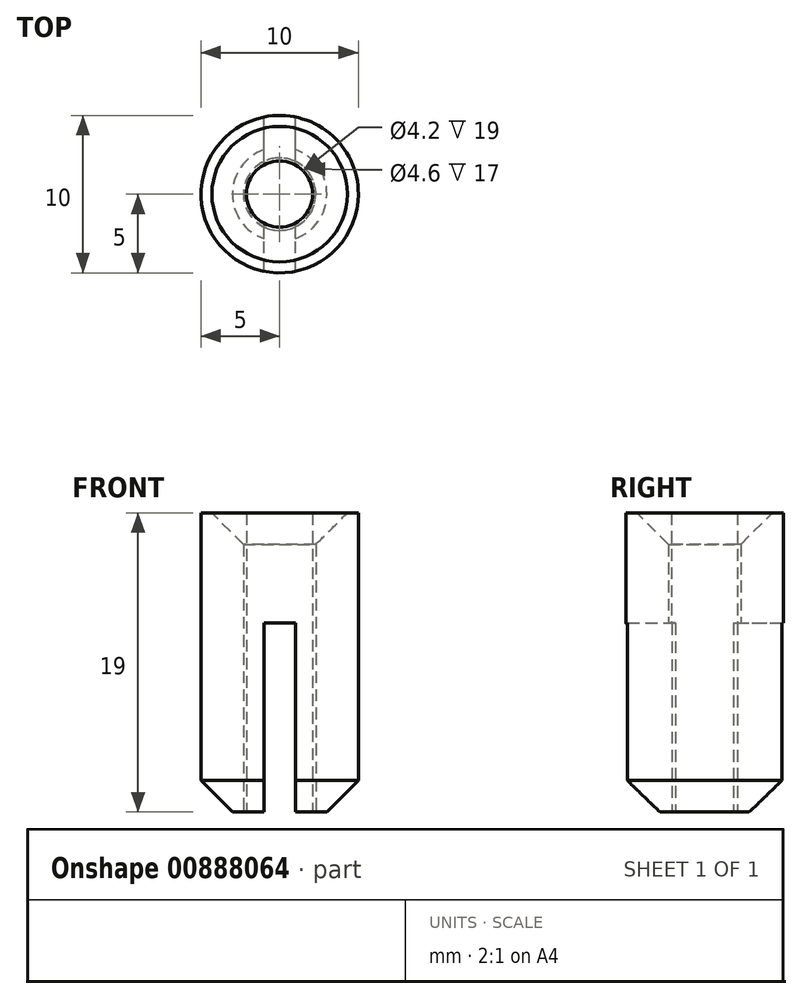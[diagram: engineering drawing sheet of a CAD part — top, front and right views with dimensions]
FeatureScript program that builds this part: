
annotation { "Feature Type Name" : "Feature", "Feature Type Description" : "" }
export const myFeature = defineFeature(function(context is Context, id is Id, definition is map)
    precondition{}
    {
        {
            var Q0;
            Q0=qCreatedBy(makeId("Top.planeOp"),FACE);
            var sketch = newSketch(context, id + "F0", { "sketchPlane" : qUnion([Q0])});
            skCircle(sketch, "E0", {"center": v(0, 0) * mm, "radius": 2.3 * mm});
            skCircle(sketch, "E1", {"center": v(0, 0) * mm, "radius": 5 * mm});
            skSolve(sketch);
        }
        {
            var Q0;
            Q0 = qSketchRegion(id + "F0", true);
            extrude(context, id + "F1", {"entities" : qUnion([Q0]), "depth" : 19 * mm, "offsetDistance" : 25 * mm});
        }
        {
            var Q0;
            Q0=makeQuery(id+"F1.opExtrude","CAP_EDGE",EDGE,{"disambiguationData":[OSD([sQuery(id+"F0.wireOp",EDGE,"E0")])],"isStart":false});
            var Q1;
            Q1=makeQuery(id+"F1.opExtrude","CAP_EDGE",EDGE,{"disambiguationData":[OSD([sQuery(id+"F0.wireOp",EDGE,"E1")])],"isStart":true});
            chamfer(context, id + "F2", {"entities" : qUnion([Q0, Q1]), "width" : 2 * mm, "tangentPropagation" : true});
        }
        {
            var Q0;
            Q0=qCreatedBy(makeId("Top.planeOp"),FACE);
            var sketch = newSketch(context, id + "F3", { "sketchPlane" : qUnion([Q0])});
            skCircle(sketch, "E2", {"center": v(0, 0) * mm, "radius": 5 * mm});
            skSolve(sketch);
        }
        {
            var Q0;
            Q0 = qSketchRegion(id + "F3", true);
            extrude(context, id + "F4", {"entities" : qUnion([Q0]), "depth" : 19 * mm, "offsetDistance" : 25 * mm});
        }
        {
            var Q0;
            Q0=makeQuery(id+"F4.opExtrude","CAP_FACE",FACE,{"disambiguationData":[OSD([sQuery(id+"F3.wireOp",EDGE,"E2")])],"isStart":false});
            var sketch = newSketch(context, id + "F5", { "sketchPlane" : qUnion([Q0])});
            skPoint(sketch, "E3", {"position": v(0, 0) * mm});
            skSolve(sketch);
        }
        {
            var Q0;
            Q0=sQuery(id+"F5.wireOp",VERTEX,"E3");
            var Q1;
            Q1=makeQuery(id+"F4.opExtrude","SWEPT_BODY",BODY,{"disambiguationData":[OSD([sQuery(id+"F3.wireOp",EDGE,"E2")])]});
            hole(context, id + "F6", {"style" : HoleStyle.SIMPLE, "endStyle" : HoleEndStyle.THROUGH, "standardTappedOrClearance" : lookupTablePath({ "standard" : "ISO", "engagement" : "75%", "pitch" : "0.8 mm", "size" : "M5", "type" : "Tapped" }), "standardBlindInLast" : lookupTablePath({ "standard" : "ISO", "fit" : "Normal", "engagement" : "75%", "pitch" : "0.8 mm", "size" : "M5", "type" : "Clearance & tapped" }), "holeDiameter" : 4.2 * mm, "majorDiameter" : 5 * mm, "showTappedDepth" : true, "isTappedThrough" : true, "tappedDepth" : 12 * mm, "tapClearance" : 3, "locations" : qUnion([Q0]), "scope" : qUnion([Q1]), "startStyle" : HoleStartStyle.PART});
        }
        {
            var Q0;
            Q0=makeQuery(id+"F6.hole-0.boolean.opBoolean","COPY",EDGE,{"derivedFrom":makeQuery(id+"F6.hole-0.opRevolve","SWEPT_EDGE",EDGE,{"disambiguationData":[OSD([sQuery(id+"F6.hole-0.sketch.wireOp",EDGE,"core_line_2"),sQuery(id+"F6.hole-0.sketch.wireOp",EDGE,"core_line_3")])]})});
            var Q1;
            Q1=makeQuery(id+"F4.opExtrude","CAP_EDGE",EDGE,{"disambiguationData":[OSD([sQuery(id+"F3.wireOp",EDGE,"E2")])],"isStart":true});
            chamfer(context, id + "F7", {"entities" : qUnion([Q0, Q1]), "width" : 2 * mm, "tangentPropagation" : true});
        }
        {
            var Q0;
            Q0=makeQuery(id+"F4.opExtrude","CAP_FACE",FACE,{"disambiguationData":[OSD([sQuery(id+"F3.wireOp",EDGE,"E2")])],"isStart":true});
            var sketch = newSketch(context, id + "F8", { "sketchPlane" : qUnion([Q0])});
            skLineSegment(sketch, "E4.bottom", {"start": v(0.5, 6) * mm, "end": v(-0.5, 6) * mm});
            skLineSegment(sketch, "E4.top", {"start": v(0.5, -6) * mm, "end": v(-0.5, -6) * mm});
            skLineSegment(sketch, "E4.left", {"start": v(0.5, 6) * mm, "end": v(0.5, -6) * mm});
            skLineSegment(sketch, "E4.right", {"start": v(-0.5, 6) * mm, "end": v(-0.5, -6) * mm});
            skPoint(sketch, "E5", {"position": v(0, -6) * mm});
            skPoint(sketch, "E6", {"position": v(0, 6) * mm});
            skPoint(sketch, "E7", {"position": v(0.5, 0) * mm});
            skPoint(sketch, "E8", {"position": v(-0.5, 0) * mm});
            skSolve(sketch);
        }
        {
            var Q0;
            Q0 = qSketchRegion(id + "F8", true);
            extrude(context, id + "F9", {"entities" : qUnion([Q0]), "operationType" : NewBodyOperationType.REMOVE, "oppositeDirection" : true, "depth" : 12 * mm, "offsetDistance" : 25 * mm});
        }
        {
            var Q0;
            Q0=makeQuery(id+"F1.opExtrude","CAP_FACE",FACE,{"disambiguationData":[OSD([sQuery(id+"F0.wireOp",EDGE,"E0"),sQuery(id+"F0.wireOp",EDGE,"E1")])],"isStart":true});
            var sketch = newSketch(context, id + "F10", { "sketchPlane" : qUnion([Q0])});
            skLineSegment(sketch, "E9.bottom", {"start": v(1, 6) * mm, "end": v(-1, 6) * mm});
            skLineSegment(sketch, "E9.top", {"start": v(1, -6) * mm, "end": v(-1, -6) * mm});
            skLineSegment(sketch, "E9.left", {"start": v(1, 6) * mm, "end": v(1, -6) * mm});
            skLineSegment(sketch, "E9.right", {"start": v(-1, 6) * mm, "end": v(-1, -6) * mm});
            skPoint(sketch, "E10", {"position": v(1, 0) * mm});
            skPoint(sketch, "E11", {"position": v(0, -6) * mm});
            skSolve(sketch);
        }
        {
            var Q0;
            Q0 = qSketchRegion(id + "F10", true);
            extrude(context, id + "F11", {"entities" : qUnion([Q0]), "operationType" : NewBodyOperationType.REMOVE, "oppositeDirection" : true, "depth" : 12 * mm, "offsetDistance" : 25 * mm});
        }
    });
